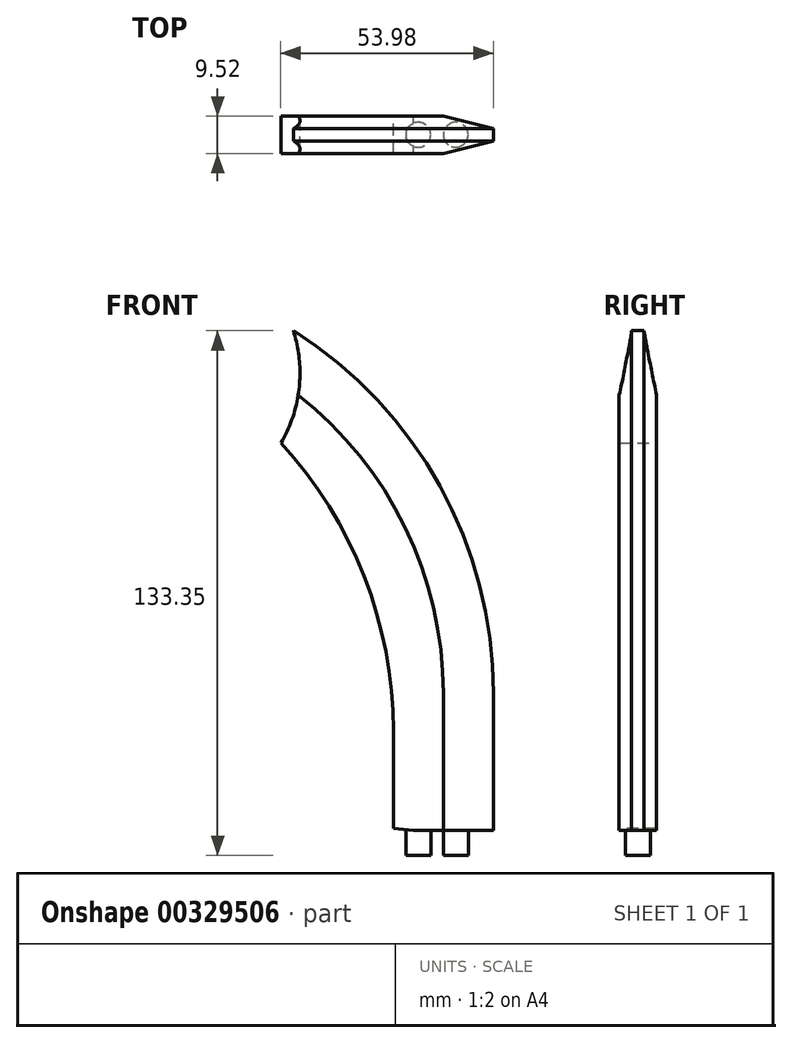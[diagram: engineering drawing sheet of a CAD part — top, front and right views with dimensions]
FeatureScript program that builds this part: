
annotation { "Feature Type Name" : "Feature", "Feature Type Description" : "" }
export const myFeature = defineFeature(function(context is Context, id is Id, definition is map)
    precondition{}
    {
        {
            var Q0;
            Q0=qCreatedBy(makeId("Front.planeOp"),FACE);
            var sketch = newSketch(context, id + "F0", { "sketchPlane" : qUnion([Q0])});
            skArc(sketch, "E0", {"start": v(-41.27, 98.43) * mm, "mid": v(-36.61, 112.37) * mm, "end": v(-38.1, 127) * mm});
            skLineSegment(sketch, "E1", {"start": v(-12.7, 0) * mm, "end": v(12.7, 0) * mm});
            skLineSegment(sketch, "E2", {"start": v(12.7, 0) * mm, "end": v(12.7, 34.92) * mm});
            skLineSegment(sketch, "E3", {"start": v(-12.7, 0) * mm, "end": v(-12.7, 25.4) * mm});
            skArc(sketch, "E4", {"start": v(12.7, 34.92) * mm, "mid": v(-0.84, 87.5) * mm, "end": v(-38.1, 127) * mm});
            skArc(sketch, "E5", {"start": v(-12.7, 25.4) * mm, "mid": v(-20.1, 64.6) * mm, "end": v(-41.27, 98.42) * mm});
            skSolve(sketch);
        }
        {
            var Q0;
            Q0=makeQuery(id+"F0.imprint","IMPRINT",FACE,{"disambiguationData":[TD([[makeQuery(id+"F0.imprint","IMPRINT",EDGE,{"derivedFrom":sQuery(id+"F0.wireOp",EDGE,"E0")}),-1.0]])]});
            extrude(context, id + "F1", {"entities" : qUnion([Q0]), "endBound" : BoundingType.SYMMETRIC, "depth" : 9.52 * mm});
        }
        {
            var Q0;
            Q0=makeQuery(id+"F1.opExtrude","CAP_EDGE",EDGE,{"disambiguationData":[OSD([sQuery(id+"F0.wireOp",EDGE,"E4")])],"isStart":false});
            var Q1;
            Q1=makeQuery(id+"F1.opExtrude","CAP_EDGE",EDGE,{"disambiguationData":[OSD([sQuery(id+"F0.wireOp",EDGE,"E2")])],"isStart":false});
            chamfer(context, id + "F2", {"entities" : qUnion([Q0, Q1]), "chamferType" : ChamferType.TWO_OFFSETS, "width1" : 3.17 * mm, "oppositeDirection" : true, "width2" : 12.7 * mm, "tangentPropagation" : true});
        }
        {
            var Q0;
            Q0=makeQuery(id+"F1.opExtrude","CAP_EDGE",EDGE,{"disambiguationData":[OSD([sQuery(id+"F0.wireOp",EDGE,"E4")])],"isStart":true});
            chamfer(context, id + "F3", {"entities" : qUnion([Q0]), "chamferType" : ChamferType.TWO_OFFSETS, "width1" : 3.17 * mm, "oppositeDirection" : false, "width2" : 12.7 * mm, "tangentPropagation" : true});
        }
        {
            var Q0;
            Q0=makeQuery(id+"F1.opExtrude","SWEPT_FACE",FACE,{"disambiguationData":[OSD([sQuery(id+"F0.wireOp",EDGE,"E1")])]});
            var sketch = newSketch(context, id + "F4", { "sketchPlane" : qUnion([Q0])});
            skCircle(sketch, "E6", {"center": v(-6.35, 0) * mm, "radius": 3.18 * mm});
            skCircle(sketch, "E7", {"center": v(3.17, 0) * mm, "radius": 3.18 * mm});
            skLineSegment(sketch, "E8", {"start": v(-6.35, 0) * mm, "end": v(3.17, 0) * mm, "construction": true});
            skSolve(sketch);
        }
        {
            var Q0;
            Q0=makeQuery(id+"F4.imprint","IMPRINT",FACE,{"disambiguationData":[TD([[makeQuery(id+"F4.imprint","IMPRINT",EDGE,{"derivedFrom":sQuery(id+"F4.wireOp",EDGE,"E6")}),1.0]])]});
            var Q1;
            Q1=makeQuery(id+"F4.imprint","IMPRINT",FACE,{"disambiguationData":[TD([[makeQuery(id+"F4.imprint","IMPRINT",EDGE,{"derivedFrom":sQuery(id+"F4.wireOp",EDGE,"E7")}),1.0]])]});
            extrude(context, id + "F5", {"entities" : qUnion([Q0, Q1]), "operationType" : NewBodyOperationType.ADD, "depth" : 6.35 * mm});
        }
        {
            var Q0;
            Q0=makeQuery(id+"F1.opExtrude","SWEPT_EDGE",EDGE,{"disambiguationData":[OSD([sQuery(id+"F0.wireOp",EDGE,"E1"),sQuery(id+"F0.wireOp",EDGE,"E3")])]});
            chamfer(context, id + "F6", {"entities" : qUnion([Q0]), "chamferType" : ChamferType.TWO_OFFSETS, "width1" : 0.5 * mm, "oppositeDirection" : true, "width2" : 5.08 * mm, "tangentPropagation" : true});
        }
    });
